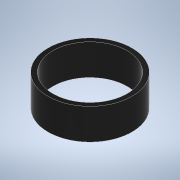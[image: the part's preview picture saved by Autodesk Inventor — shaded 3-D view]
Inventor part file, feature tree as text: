
AUTODESK INVENTOR PART (.ipt)
format: ipt  version: 2022 (Build 260153000, 153)  size: 98,816 bytes
history: native  units: in
note: dims shown in document units (in); Inventor stores cm internally (conversion verified against a paired STEP export)
features: extrude x1, sketch x1
ambient origin geometry x8: Origin, YZ Plane, XZ Plane, XY Plane, X Axis, Y Axis, Z Axis, Center Point
bodies: Solid1 (feature_tree)
feature tree (2):
  extrude  "Extrusion1"  Depth=0.5118in
  sketch  "Sketch1"  dims[d0=1.3878in d1=0.0787in d2=0.5118in d3=0.0in]
